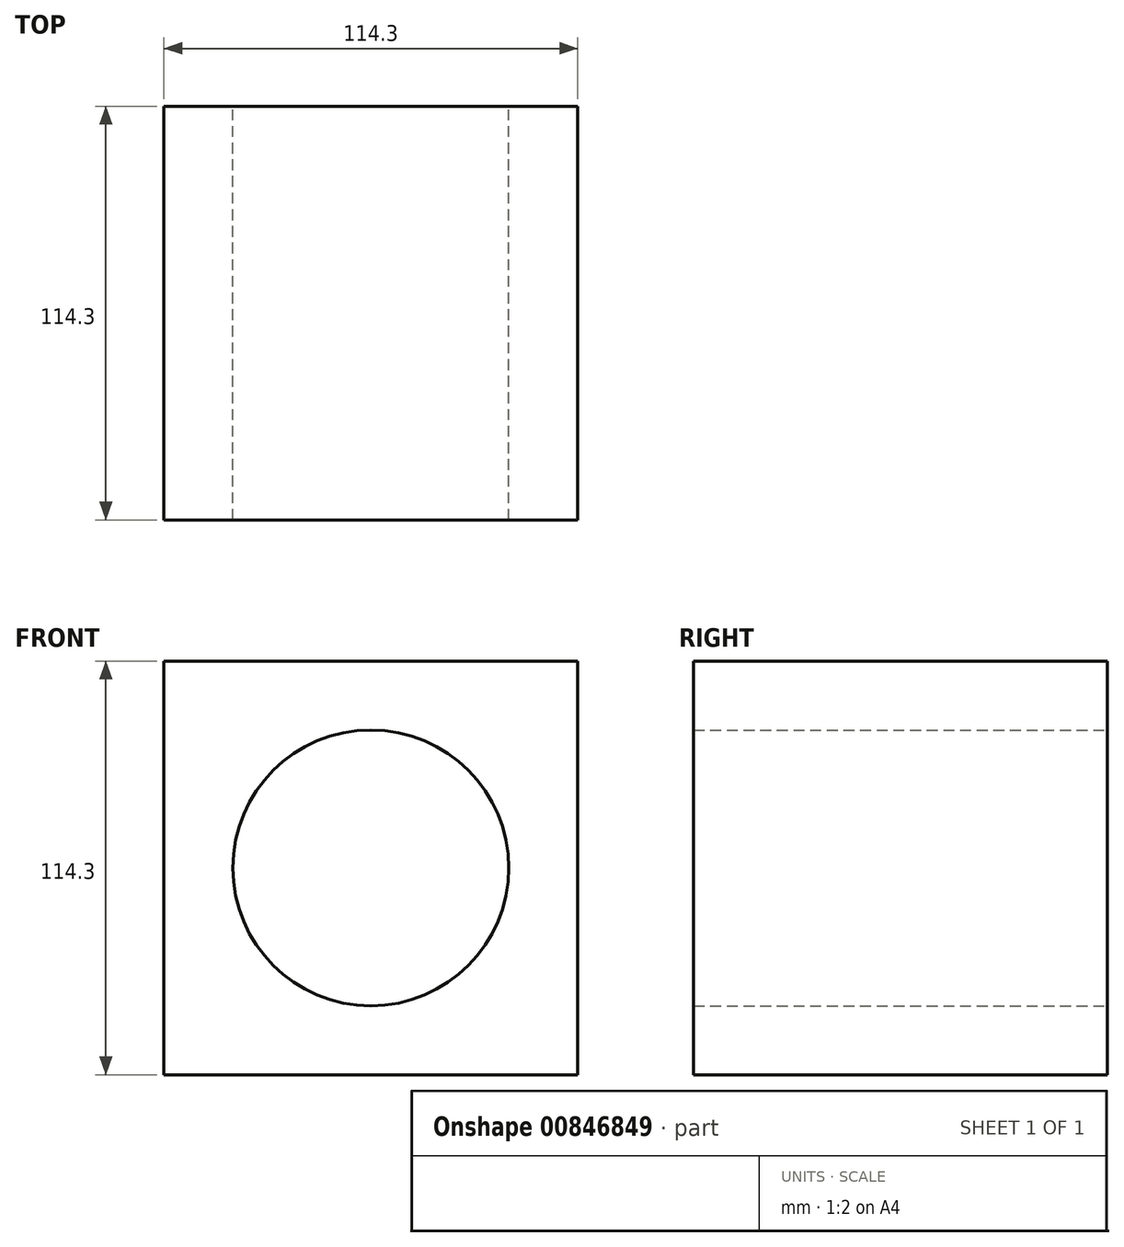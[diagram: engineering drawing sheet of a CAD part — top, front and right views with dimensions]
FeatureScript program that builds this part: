
annotation { "Feature Type Name" : "Feature", "Feature Type Description" : "" }
export const myFeature = defineFeature(function(context is Context, id is Id, definition is map)
    precondition{}
    {
        {
            var Q0;
            Q0=qCreatedBy(makeId("Front.planeOp"),FACE);
            var sketch = newSketch(context, id + "F0", { "sketchPlane" : qUnion([Q0])});
            skLineSegment(sketch, "E0.bottom", {"start": v(-57.15, 57.15) * mm, "end": v(57.15, 57.15) * mm});
            skLineSegment(sketch, "E0.top", {"start": v(-57.15, -57.15) * mm, "end": v(57.15, -57.15) * mm});
            skLineSegment(sketch, "E0.left", {"start": v(-57.15, 57.15) * mm, "end": v(-57.15, -57.15) * mm});
            skLineSegment(sketch, "E0.right", {"start": v(57.15, 57.15) * mm, "end": v(57.15, -57.15) * mm});
            skLineSegment(sketch, "E1", {"start": v(-57.15, -57.15) * mm, "end": v(57.15, 57.15) * mm});
            skCircle(sketch, "E2", {"center": v(0, 0) * mm, "radius": 38.1 * mm});
            skSolve(sketch);
        }
        {
            var Q0;
            Q0 = qSketchRegion(id + "F0", true);
            extrude(context, id + "F1", {"entities" : qUnion([Q0]), "depth" : 114.3 * mm, "offsetDistance" : 25.4 * mm, "symmetric" : true});
        }
    });
